# Revit family: TapSet_Shower_Nero_Mecca_Divertor_Split
name_source: partatom
category: Plumbing Fixtures
units: mm (PartAtom-declared; Revit-internal decimal feet)

## family parameters
Always vertical = Yes
Cut with Voids When Loaded = Yes
Maintain Annotation Orientation = No
OmniClass Number = 23.31.11.19
Part Type = Normal
Room Calculation Point = No
Round Connector Dimension = Use Diameter
Shared = No
Work Plane-Based = No

## types (7) — shared parameters
Assembly Code = C1030210
CW Connection = Yes
Description = Mecca Shower Mixer Divertor System Separate Back Plate
HW Connection = Yes
IfcExportAs = ifcValve
IfcExportType = FAUCET
Manufacturer = Nero
ManufacturerOverallDepth = 97.8 mm
ManufacturerOverallHeight = 310.6 mm
ManufacturerOverallWidth = 225 mm
ManufacturerURLProductSpecific = https://nerotapware.com.au
ModifiedIssue = 20231106 $
URL = https://nerotapware.com.au
Uniclass2015Code = Pr_40_20_87_55
Uniclass2015Title = Mixer taps
Uniclass2015Version = Products v1.28
Vent Connection = No
Waste Connection = No
zero-valued in all types: Default Elevation

## per-type parameters (varying)
| type | BodyMaterial | ManufacturerSpecCode | Model | Type Comments |
| Matte White (NR221912fMW) | Metal_MatteWhite_Nero | NR221912fMW | NR221912fMW | Tap Set - Shower - Divertor - Split - Matte White |
| Matte Black (NR221912fMB) | Metal_MatteBlack_Nero | NR221912fMW | NR221912fMW | Tap Set - Shower - Divertor - Split - Matte Black |
| Gun Metal (NR221912fGM) | Metal_GunMetal_Nero | NR221912fMB | NR221912fMB | Tap Set - Shower - Divertor - Split - Gun Metal |
| Chrome (NR221912fCH) | Metal_Chrome_Nero | NR221912fCH | NR221912fCH | Tap Set - Shower - Divertor - Split - Chrome |
| Brushed Bronze (NR221912fBZ) | Metal_Bronze_Nero_Brushed | NR221912fBZ | NR221912fBZ | Tap Set - Shower - Divertor - Split - Brushed Bronze |
| Brushed Nickel (NR221912fBN) | Metal_Nickel_Nero_Brushed | NR221912fBG | NR221912fBG | Tap Set - Shower - Divertor - Split - Brushed Nickel |
| Brushed Gold (NR221912fBG) | Metal_Gold_Nero_Brushed | NR221912fBG | NR221912fBG | Tap Set - Shower - Divertor - Split - Brushed Gold |

## geometry (parser evidence)
native form markers: Sweep x2
no freeform markers — native parametric forms only
